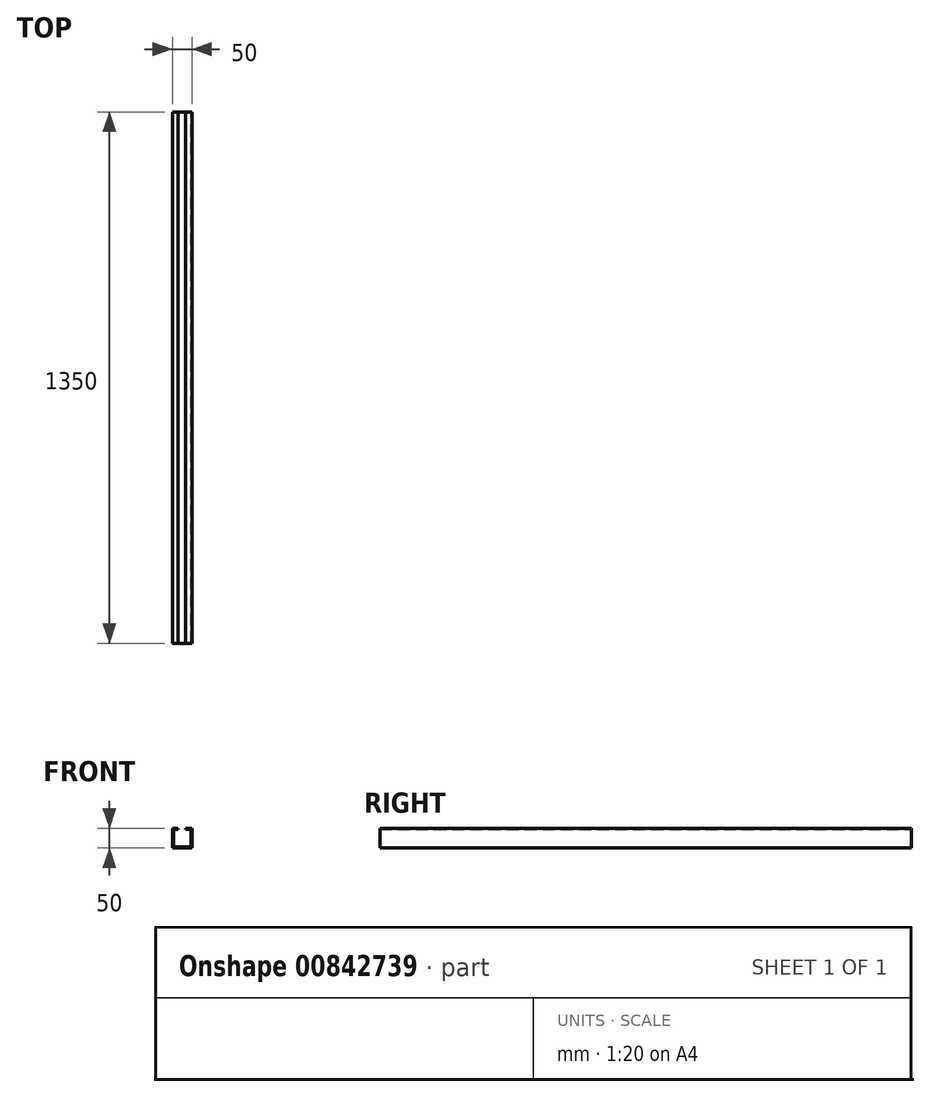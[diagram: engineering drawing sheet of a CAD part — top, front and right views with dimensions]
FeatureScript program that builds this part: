
annotation { "Feature Type Name" : "Feature", "Feature Type Description" : "" }
export const myFeature = defineFeature(function(context is Context, id is Id, definition is map)
    precondition{}
    {
        {
            var Q0;
            Q0=qCreatedBy(makeId("Front.planeOp"),FACE);
            var sketch = newSketch(context, id + "F0", { "sketchPlane" : qUnion([Q0])});
            skLineSegment(sketch, "E0.bottom", {"start": v(25, -25) * mm, "end": v(-25, -25) * mm});
            skLineSegment(sketch, "E0.top", {"start": v(25, 25) * mm, "end": v(-25, 25) * mm});
            skLineSegment(sketch, "E0.left", {"start": v(25, -25) * mm, "end": v(25, 25) * mm});
            skLineSegment(sketch, "E0.right", {"start": v(-25, -25) * mm, "end": v(-25, 25) * mm});
            skPoint(sketch, "E0.middle", {"position": v(0, 0) * mm});
            skLineSegment(sketch, "E1.0", {"start": v(22, 22) * mm, "end": v(-22, 22) * mm});
            skLineSegment(sketch, "E1.1", {"start": v(22, -22) * mm, "end": v(22, 22) * mm});
            skLineSegment(sketch, "E1.2", {"start": v(22, -22) * mm, "end": v(-22, -22) * mm});
            skLineSegment(sketch, "E1.3", {"start": v(-22, -22) * mm, "end": v(-22, 22) * mm});
            skLineSegment(sketch, "E2.bottom", {"start": v(0, 22) * mm, "end": v(-10, 22) * mm});
            skLineSegment(sketch, "E2.top", {"start": v(0, 25) * mm, "end": v(-10, 25) * mm});
            skLineSegment(sketch, "E2.left", {"start": v(0, 22) * mm, "end": v(0, 25) * mm});
            skLineSegment(sketch, "E2.right", {"start": v(-10, 22) * mm, "end": v(-10, 25) * mm});
            skLineSegment(sketch, "E3.bottom", {"start": v(0, 22) * mm, "end": v(8.4, 22) * mm});
            skLineSegment(sketch, "E3.top", {"start": v(0, 25) * mm, "end": v(8.4, 25) * mm});
            skLineSegment(sketch, "E3.right", {"start": v(8.4, 22) * mm, "end": v(8.4, 25) * mm});
            skSolve(sketch);
        }
        {
            var Q0;
            Q0=makeQuery(id+"F0.imprint","IMPRINT",FACE,{"disambiguationData":[TD([[makeQuery(id+"F0.imprint","IMPRINT",EDGE,{"derivedFrom":sQuery(id+"F0.wireOp",EDGE,"E0.bottom")}),-1.0]])]});
            extrude(context, id + "F1", {"entities" : qUnion([Q0]), "depth" : 1350 * mm, "offsetDistance" : 25 * mm});
        }
    });
